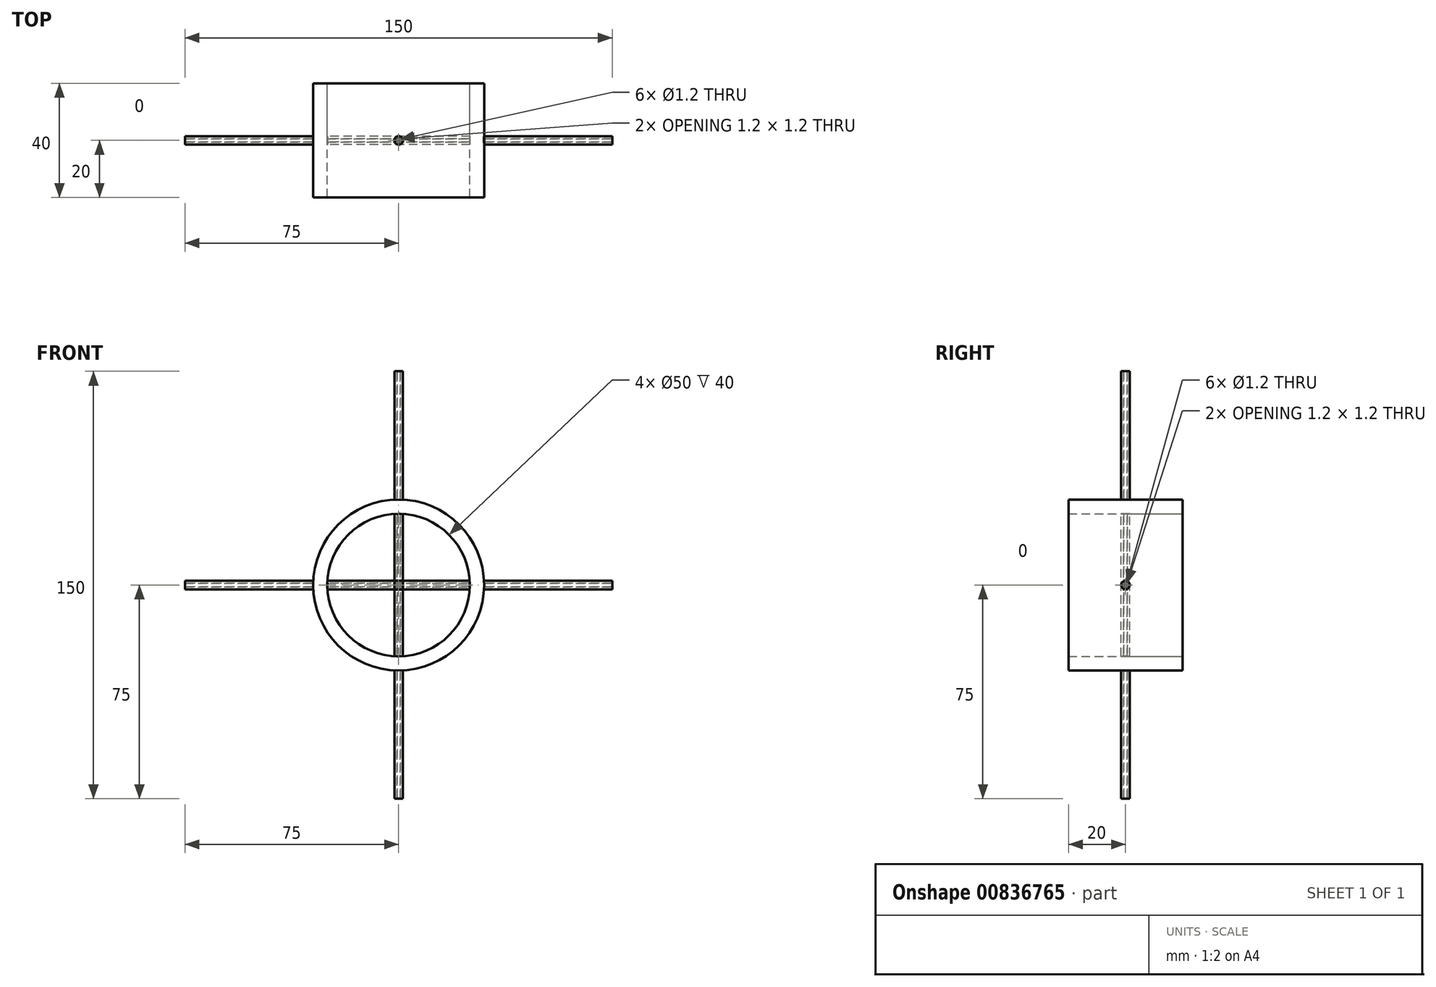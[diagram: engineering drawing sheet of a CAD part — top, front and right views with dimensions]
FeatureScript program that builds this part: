
annotation { "Feature Type Name" : "Feature", "Feature Type Description" : "" }
export const myFeature = defineFeature(function(context is Context, id is Id, definition is map)
    precondition{}
    {
        {
            var Q0;
            Q0=qCreatedBy(makeId("Front.planeOp"),FACE);
            var sketch = newSketch(context, id + "F0", { "sketchPlane" : qUnion([Q0])});
            skCircle(sketch, "E0", {"center": v(0, 0) * mm, "radius": 30 * mm});
            skCircle(sketch, "E1", {"center": v(0, 0) * mm, "radius": 25 * mm});
            skSolve(sketch);
        }
        {
            var Q0;
            Q0=makeQuery(id+"F0.imprint","IMPRINT",FACE,{"disambiguationData":[TD([[makeQuery(id+"F0.imprint","IMPRINT",EDGE,{"derivedFrom":sQuery(id+"F0.wireOp",EDGE,"E0")}),1.0]])]});
            var Q1;
            Q1=sQuery(id+"F0.wireOp",EDGE,"E1");
            var Q2;
            Q2=sQuery(id+"F0.wireOp",EDGE,"E0");
            extrude(context, id + "F1", {"entities" : qUnion([Q0]), "surfaceEntities" : qUnion([Q1, Q2]), "endBound" : BoundingType.SYMMETRIC, "depth" : 40 * mm, "offsetDistance" : 25.4 * mm});
        }
        {
            var Q0;
            Q0=qCreatedBy(makeId("Top.planeOp"),FACE);
            var sketch = newSketch(context, id + "F2", { "sketchPlane" : qUnion([Q0])});
            skCircle(sketch, "E2", {"center": v(0, 0) * mm, "radius": 1.5 * mm});
            skCircle(sketch, "E3", {"center": v(0, 0) * mm, "radius": 0.6 * mm});
            skSolve(sketch);
        }
        {
            var Q0;
            Q0 = qSketchRegion(id + "F2", true);
            extrude(context, id + "F3", {"entities" : qUnion([Q0]), "operationType" : NewBodyOperationType.ADD, "endBound" : BoundingType.SYMMETRIC, "depth" : 150 * mm, "offsetDistance" : 25.4 * mm});
        }
        {
            var Q0;
            Q0=qCreatedBy(makeId("Right.planeOp"),FACE);
            var sketch = newSketch(context, id + "F4", { "sketchPlane" : qUnion([Q0])});
            skLineSegment(sketch, "E4", {"start": v(-31.14, 0) * mm, "end": v(38.09, 0) * mm});
            skSolve(sketch);
        }
        {
            var Q0;
            Q0=makeQuery(id+"F1.opExtrude","SWEPT_BODY",BODY,{"disambiguationData":[OSD([sQuery(id+"F0.wireOp",EDGE,"E0"),sQuery(id+"F0.wireOp",EDGE,"E1")])]});
            var Q1;
            Q1=sQuery(id+"F4.wireOp",EDGE,"E4");
            circularPattern(context, id + "F5", {"entities" : qUnion([Q0]), "axis" : qUnion([Q1]), "angle" : 360 * degree, "instanceCount" : 4, "equalSpace" : true});
        }
    });
